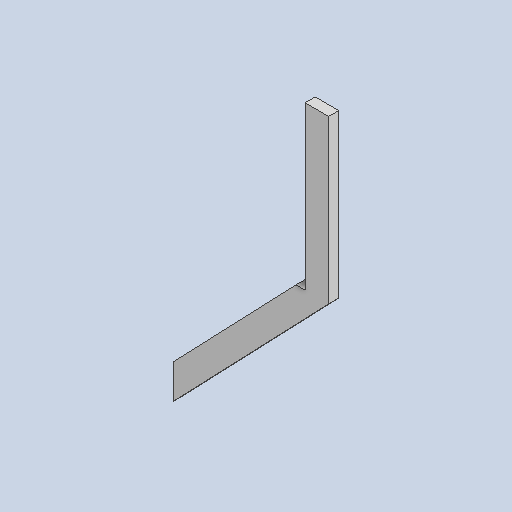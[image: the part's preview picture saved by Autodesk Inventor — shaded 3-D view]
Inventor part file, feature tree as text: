
AUTODESK INVENTOR PART (.ipt)
format: ipt  version: 2025 (Build 290162000, 162)  size: 82,432 bytes
history: native  units: in
note: dims shown in document units (in); Inventor stores cm internally (conversion verified against a paired STEP export)
features: other x3, sketch x1
ambient origin geometry x8: Origin, YZ Plane, XZ Plane, XY Plane, X Axis, Y Axis, Z Axis, Center Point
bodies: Solid1 (feature_tree)
feature tree (4):
  other  "back_side_MIR.ipt"
  other  "Solid1::back_side_MIR.ipt"
  other  "TaggingFeature1"
  sketch  "Sketch1"  dims[d0=0.3937in]
